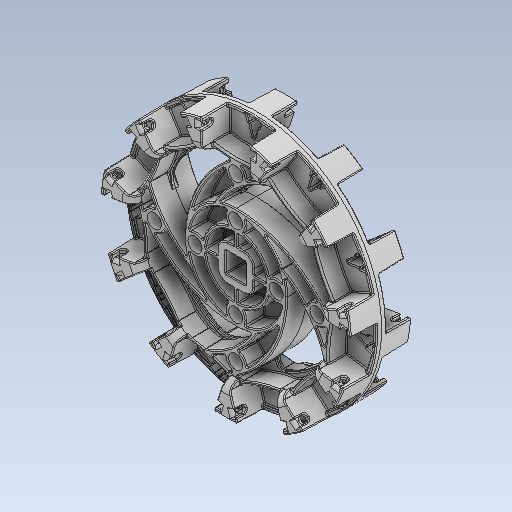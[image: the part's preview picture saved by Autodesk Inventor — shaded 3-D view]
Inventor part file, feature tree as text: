
AUTODESK INVENTOR PART (.ipt)
format: ipt  version: 2020 (Build 240168000, 168)  size: 10,479,616 bytes
history: native  units: in
note: dims shown in document units (in); Inventor stores cm internally (conversion verified against a paired STEP export)
features: chamfer x1
ambient origin geometry x8: Origin, YZ Plane, XZ Plane, XY Plane, X Axis, Y Axis, Z Axis, Center Point
bodies: Solid1 (feature_tree)
feature tree (1):
  chamfer  "Chamfer2"  [1 undecoded]
note: 1 required parameter value undecoded (feature->parameter linkage not recoverable at this tier; creation-order binding heuristic only, values carry confidence <= 0.55)
